# Revit family: Zaniboni-Diva-5_Inch_Pendant-1
name_source: partatom
category: Lighting Fixtures
revit_build: Autodesk Revit 2016 (Build: 20150220_1215(x64)
units: mm (PartAtom-declared; Revit-internal decimal feet)

## family parameters
Cut with Voids When Loaded = No
Host = Face
Light Source = No
Part Type = Normal
Room Calculation Point = No
Round Connector Dimension = Use Diameter
Shared = No

## types (1)
- Type Catalog
    Assembly Code = E1020300
    Base Finish = ZBN - Metal Matte White
    Beam = 36°
    Body Finish = ZBN - Metal Matte White
    CRI = 80
    Cable = Yes
    Cable Finish = ZBN - Chrome
    Cable Width = 0"
    Cc = No
    Cd = 3"
    Cord = No
    Cord Finish = ZBN - Chrome
    Ct = No
    Cw = 1 1/2"
    D = No
    Default Elevation = 1"
    Depth Base = 6"
    Description = Type Catalog
    Diffuser Finish = ZBN - Metal Matte White
    Fd = 61/64"
    Frame Finish = ZBN - Metal Matte White
    Fw = 61/64"
    Kelvin = 3000°K
    Keynote = 12500
    Length = 6"
    Manufacturer = Zaniboni
    Mechanism Finish = ZBN - Plastic-Black
    Model = Type Catalog
    Q = No
    SD = No
    SQ = No
    ST = No
    Screen Finish = ZBN - Glass
    Support Finish = ZBN - Metal Matte White
    T = No
    Type Comments = Diva
    URL = www.zanibonilighting.com
    Voltage = 120 V
    Wattage Comments = 14W
    Width = 6"
    Width Base = 6"

## geometry (parser evidence)
native form markers: Sweep x5
no freeform markers — native parametric forms only
